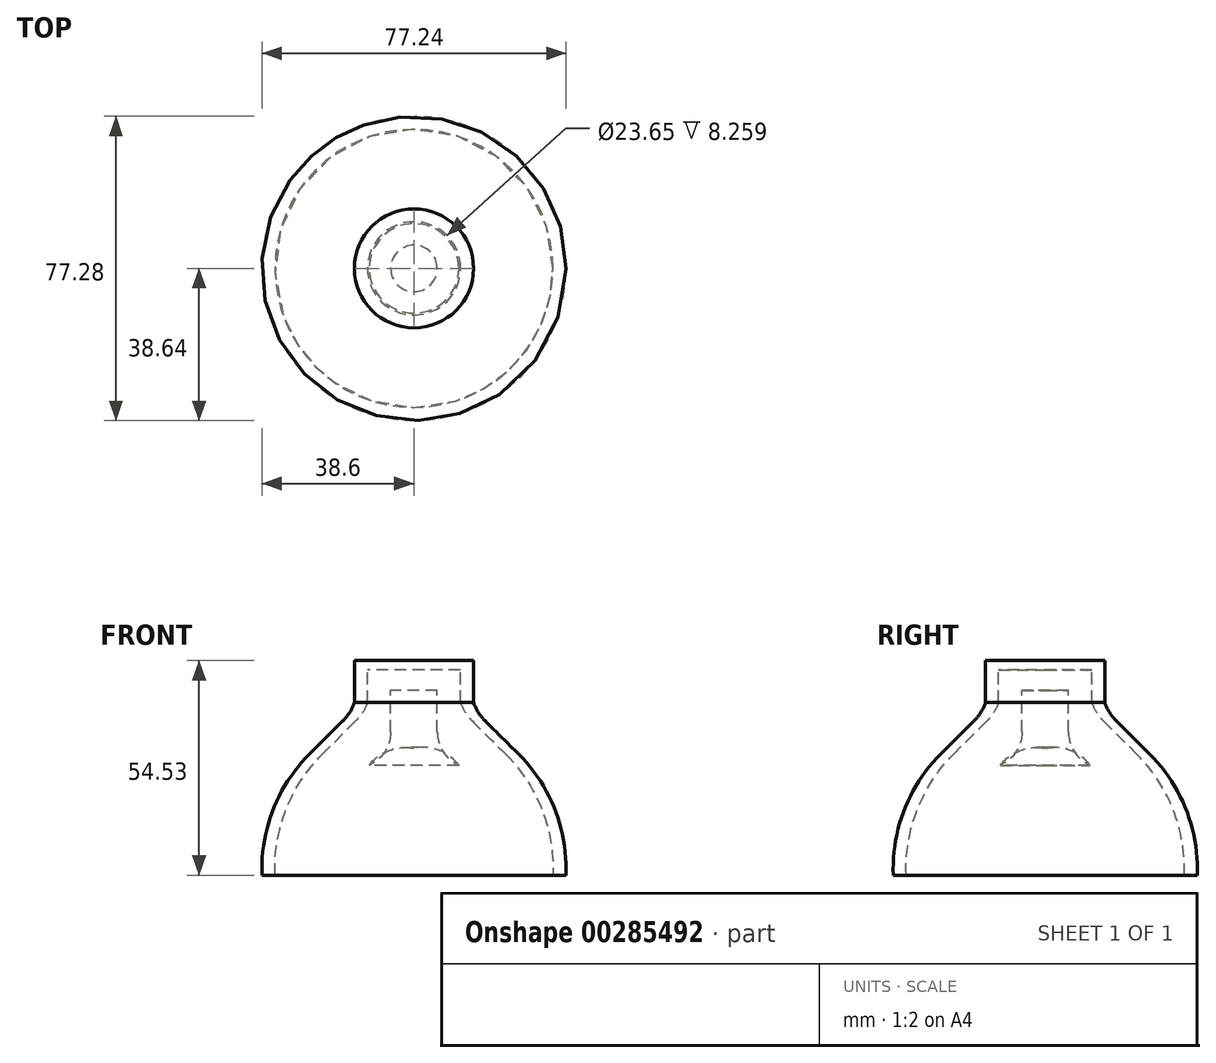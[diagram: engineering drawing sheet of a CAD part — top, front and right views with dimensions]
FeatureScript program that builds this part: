
annotation { "Feature Type Name" : "Feature", "Feature Type Description" : "" }
export const myFeature = defineFeature(function(context is Context, id is Id, definition is map)
    precondition{}
    {
        {
            var Q0;
            Q0=qCreatedBy(makeId("Front.planeOp"),FACE);
            var sketch = newSketch(context, id + "F0", { "sketchPlane" : qUnion([Q0])});
            skArc(sketch, "E0", {"start": v(-26.5, 30.82) * mm, "mid": v(-35.8, 16.68) * mm, "end": v(-38.6, 0) * mm});
            skLineSegment(sketch, "E1", {"start": v(-26.5, 30.82) * mm, "end": v(-18.13, 39.14) * mm});
            skArc(sketch, "E2", {"start": v(-18.13, 39.14) * mm, "mid": v(-16.36, 41.34) * mm, "end": v(-15.13, 43.88) * mm});
            skLineSegment(sketch, "E3", {"start": v(-15.13, 43.88) * mm, "end": v(-15.13, 54.53) * mm});
            skLineSegment(sketch, "E4", {"start": v(-15.13, 54.53) * mm, "end": v(0, 54.53) * mm});
            skLineSegment(sketch, "E5", {"start": v(-35.3, 0) * mm, "end": v(-38.6, 0) * mm});
            skArc(sketch, "E6", {"start": v(-23.2, 30.82) * mm, "mid": v(-32.5, 16.68) * mm, "end": v(-35.3, 0) * mm});
            skLineSegment(sketch, "E7", {"start": v(-23.2, 30.82) * mm, "end": v(-14.82, 39.14) * mm});
            skArc(sketch, "E8", {"start": v(-14.82, 39.14) * mm, "mid": v(-13.06, 41.34) * mm, "end": v(-11.83, 43.88) * mm});
            skLineSegment(sketch, "E9", {"start": v(-11.83, 43.88) * mm, "end": v(-11.83, 52.14) * mm});
            skLineSegment(sketch, "E10", {"start": v(-11.83, 54.53) * mm, "end": v(0, 54.53) * mm});
            skLineSegment(sketch, "E11", {"start": v(-11.83, 52.14) * mm, "end": v(0, 52.14) * mm});
            skLineSegment(sketch, "E12", {"start": v(0, 46.96) * mm, "end": v(-5.91, 46.96) * mm});
            skPoint(sketch, "E12.endSnap0", {"position": v(-5.91, 52.14) * mm});
            skLineSegment(sketch, "E13", {"start": v(-5.91, 46.96) * mm, "end": v(-5.91, 36.45) * mm});
            skArc(sketch, "E14", {"start": v(-11.38, 27.93) * mm, "mid": v(-7.4, 31.39) * mm, "end": v(-5.91, 36.45) * mm});
            skArc(sketch, "E15", {"start": v(-11.38, 27.93) * mm, "mid": v(-12, 14.85) * mm, "end": v(0, 9.61) * mm});
            skLineSegment(sketch, "E16", {"start": v(0, 54.53) * mm, "end": v(0, 52.14) * mm});
            skLineSegment(sketch, "E17", {"start": v(0, 46.96) * mm, "end": v(0, 9.61) * mm});
            skSolve(sketch);
        }
        {
            var Q0;
            Q0=makeQuery(id+"F0.imprint","IMPRINT",FACE,{"disambiguationData":[TD([[makeQuery(id+"F0.imprint","IMPRINT",EDGE,{"derivedFrom":sQuery(id+"F0.wireOp",EDGE,"E0")}),1.0]])]});
            var Q1;
            Q1=makeQuery(id+"F0.imprint","IMPRINT",FACE,{"disambiguationData":[TD([[makeQuery(id+"F0.imprint","IMPRINT",EDGE,{"derivedFrom":sQuery(id+"F0.wireOp",EDGE,"E12")}),1.0]])]});
            var Q2;
            Q2=sQuery(id+"F0.wireOp",EDGE,"E17");
            revolve(context, id + "F1", {"entities" : qUnion([Q0, Q1]), "axis" : qUnion([Q2]), "revolveType" : RevolveType.FULL});
        }
    });
